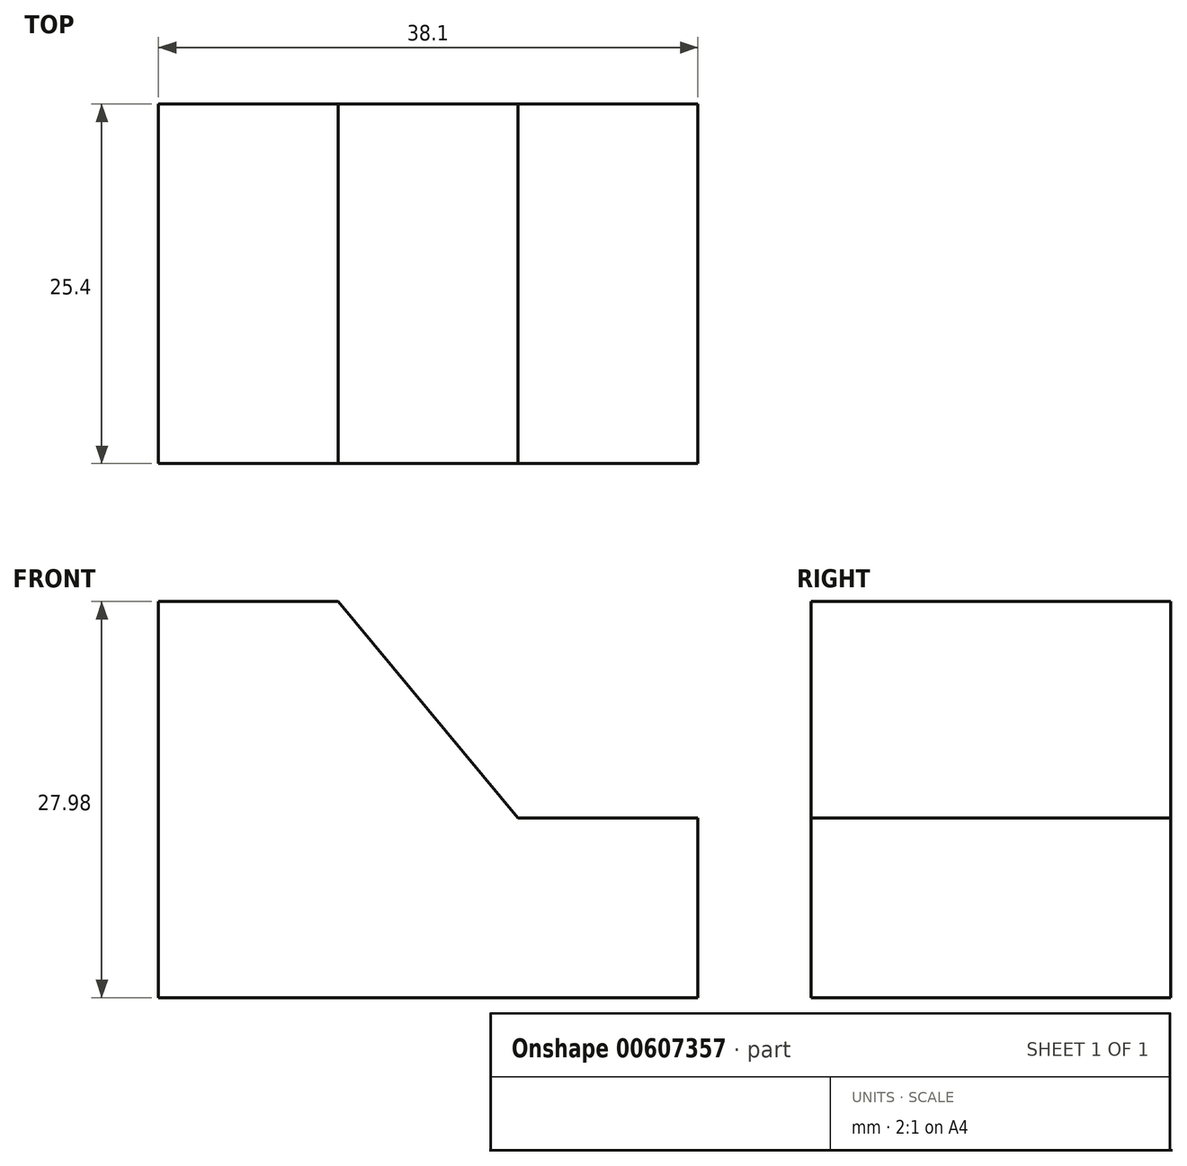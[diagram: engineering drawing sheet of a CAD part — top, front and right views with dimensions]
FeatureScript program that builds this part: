
annotation { "Feature Type Name" : "Feature", "Feature Type Description" : "" }
export const myFeature = defineFeature(function(context is Context, id is Id, definition is map)
    precondition{}
    {
        {
            var Q0;
            Q0=qCreatedBy(makeId("Front.planeOp"),FACE);
            var sketch = newSketch(context, id + "F0", { "sketchPlane" : qUnion([Q0])});
            skLineSegment(sketch, "E0", {"start": v(0, -3.77) * mm, "end": v(0, 27.98) * mm});
            skLineSegment(sketch, "E1", {"start": v(0, 27.98) * mm, "end": v(12.7, 27.98) * mm});
            skLineSegment(sketch, "E2", {"start": v(0, 0) * mm, "end": v(38.1, 0) * mm});
            skLineSegment(sketch, "E3", {"start": v(38.1, 0) * mm, "end": v(38.1, 12.7) * mm});
            skLineSegment(sketch, "E4", {"start": v(38.1, 12.7) * mm, "end": v(25.4, 12.7) * mm});
            skLineSegment(sketch, "E5", {"start": v(25.4, 12.7) * mm, "end": v(12.7, 27.98) * mm});
            skSolve(sketch);
        }
        {
            var Q0;
            {var subQ1=sQuery(id+"F0.wireOp",EDGE,"E1");Q0=makeQuery(id+"F0.imprint","IMPRINT",FACE,{"disambiguationData":[TD([[makeQuery(id+"F0.imprint","IMPRINT",EDGE,{"derivedFrom":subQ1}),-1.0]])]});}
            extrude(context, id + "F1", {"entities" : qUnion([Q0]), "depth" : 25.4 * mm, "offsetDistance" : 25.4 * mm});
        }
    });
